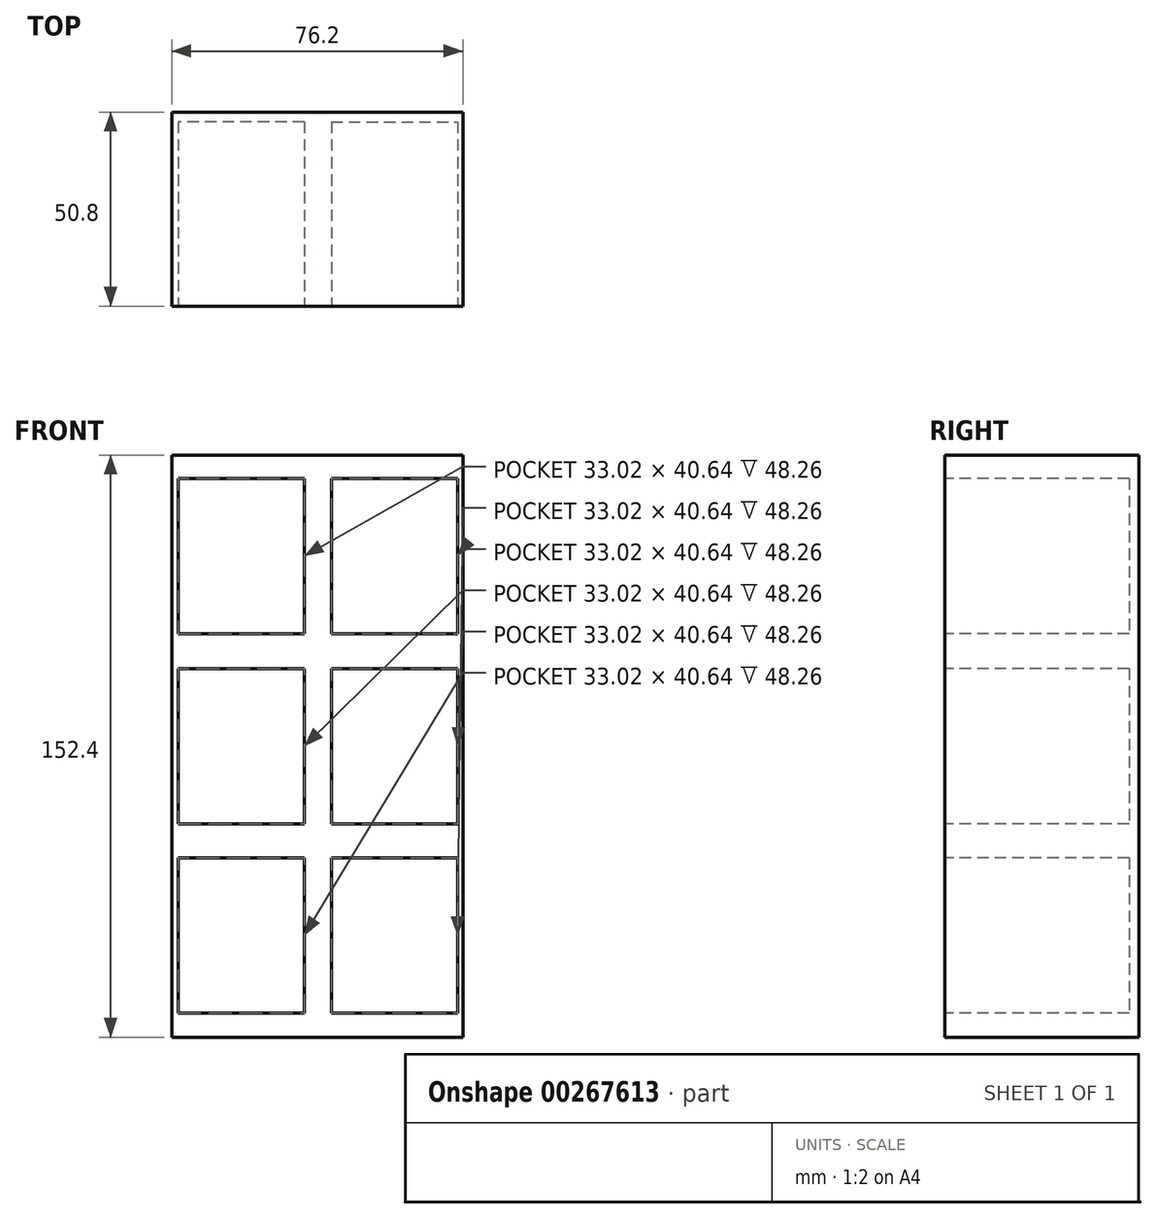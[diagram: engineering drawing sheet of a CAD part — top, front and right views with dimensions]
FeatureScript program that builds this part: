
annotation { "Feature Type Name" : "Feature", "Feature Type Description" : "" }
export const myFeature = defineFeature(function(context is Context, id is Id, definition is map)
    precondition{}
    {
        {
            var Q0;
            Q0=qCreatedBy(makeId("Front.planeOp"),FACE);
            var sketch = newSketch(context, id + "F0", { "sketchPlane" : qUnion([Q0])});
            skLineSegment(sketch, "E0.bottom", {"start": v(38.1, 76.2) * mm, "end": v(-38.1, 76.2) * mm});
            skLineSegment(sketch, "E0.top", {"start": v(38.1, -76.2) * mm, "end": v(-38.1, -76.2) * mm});
            skLineSegment(sketch, "E0.left", {"start": v(38.1, 76.2) * mm, "end": v(38.1, -76.2) * mm});
            skLineSegment(sketch, "E0.right", {"start": v(-38.1, 76.2) * mm, "end": v(-38.1, -76.2) * mm});
            skPoint(sketch, "E0.middle", {"position": v(0, 0) * mm});
            skSolve(sketch);
        }
        {
            var Q0;
            Q0 = qSketchRegion(id + "F0", true);
            extrude(context, id + "F1", {"entities" : qUnion([Q0]), "depth" : 50.8 * mm});
        }
        {
            var Q0;
            Q0=makeQuery(id+"F1.opExtrude","CAP_FACE",FACE,{"disambiguationData":[OSD([sQuery(id+"F0.wireOp",EDGE,"E0.bottom"),sQuery(id+"F0.wireOp",EDGE,"E0.top"),sQuery(id+"F0.wireOp",EDGE,"E0.left"),sQuery(id+"F0.wireOp",EDGE,"E0.right")])],"isStart":false});
            var sketch = newSketch(context, id + "F2", { "sketchPlane" : qUnion([Q0])});
            skLineSegment(sketch, "E1.bottom", {"start": v(-3.37, 70.1) * mm, "end": v(-36.4, 70.1) * mm});
            skLineSegment(sketch, "E1.top", {"start": v(-3.37, 29.47) * mm, "end": v(-36.4, 29.47) * mm});
            skLineSegment(sketch, "E1.left", {"start": v(-3.37, 70.1) * mm, "end": v(-3.37, 29.47) * mm});
            skLineSegment(sketch, "E1.right", {"start": v(-36.4, 70.1) * mm, "end": v(-36.4, 29.47) * mm});
            skPoint(sketch, "E1.middle", {"position": v(-19.88, 49.79) * mm});
            skLineSegment(sketch, "E2.bottom", {"start": v(3.7, 70.1) * mm, "end": v(36.72, 70.1) * mm});
            skLineSegment(sketch, "E2.top", {"start": v(3.7, 29.47) * mm, "end": v(36.72, 29.47) * mm});
            skLineSegment(sketch, "E2.left", {"start": v(3.7, 70.1) * mm, "end": v(3.7, 29.47) * mm});
            skLineSegment(sketch, "E2.right", {"start": v(36.72, 70.1) * mm, "end": v(36.72, 29.47) * mm});
            skPoint(sketch, "E2.middle", {"position": v(20.21, 49.79) * mm});
            skLineSegment(sketch, "E3.bottom", {"start": v(-3.37, 20.32) * mm, "end": v(-36.4, 20.32) * mm});
            skLineSegment(sketch, "E3.top", {"start": v(-3.37, -20.32) * mm, "end": v(-36.4, -20.32) * mm});
            skLineSegment(sketch, "E3.left", {"start": v(-3.37, 20.32) * mm, "end": v(-3.37, -20.32) * mm});
            skLineSegment(sketch, "E3.right", {"start": v(-36.4, 20.32) * mm, "end": v(-36.4, -20.32) * mm});
            skPoint(sketch, "E3.middle", {"position": v(-19.88, 0) * mm});
            skLineSegment(sketch, "E4.bottom", {"start": v(3.7, 20.32) * mm, "end": v(36.72, 20.32) * mm});
            skLineSegment(sketch, "E4.top", {"start": v(3.7, -20.32) * mm, "end": v(36.72, -20.32) * mm});
            skLineSegment(sketch, "E4.left", {"start": v(3.7, 20.32) * mm, "end": v(3.7, -20.32) * mm});
            skLineSegment(sketch, "E4.right", {"start": v(36.72, 20.32) * mm, "end": v(36.72, -20.32) * mm});
            skPoint(sketch, "E4.middle", {"position": v(20.21, 0) * mm});
            skPoint(sketch, "E4.middle.positionSnap0", {"position": v(20.21, 29.47) * mm});
            skPoint(sketch, "E4.centerSnap0", {"position": v(20.21, 29.47) * mm});
            skLineSegment(sketch, "E5.bottom", {"start": v(-3.37, -29.28) * mm, "end": v(-36.4, -29.28) * mm});
            skLineSegment(sketch, "E5.top", {"start": v(-3.37, -69.92) * mm, "end": v(-36.4, -69.92) * mm});
            skLineSegment(sketch, "E5.left", {"start": v(-3.37, -29.28) * mm, "end": v(-3.37, -69.92) * mm});
            skLineSegment(sketch, "E5.right", {"start": v(-36.4, -29.28) * mm, "end": v(-36.4, -69.92) * mm});
            skPoint(sketch, "E5.middle", {"position": v(-19.88, -49.6) * mm});
            skLineSegment(sketch, "E6.bottom", {"start": v(3.7, -29.28) * mm, "end": v(36.72, -29.28) * mm});
            skLineSegment(sketch, "E6.top", {"start": v(3.7, -69.92) * mm, "end": v(36.72, -69.92) * mm});
            skLineSegment(sketch, "E6.left", {"start": v(3.7, -29.28) * mm, "end": v(3.7, -69.92) * mm});
            skLineSegment(sketch, "E6.right", {"start": v(36.72, -29.28) * mm, "end": v(36.72, -69.92) * mm});
            skPoint(sketch, "E6.middle", {"position": v(20.21, -49.6) * mm});
            skPoint(sketch, "E6.middle.positionSnap0", {"position": v(20.21, -20.32) * mm});
            skPoint(sketch, "E6.centerSnap0", {"position": v(20.21, -20.32) * mm});
            skSolve(sketch);
        }
        {
            var Q0;
            Q0 = qSketchRegion(id + "F2", true);
            extrude(context, id + "F3", {"entities" : qUnion([Q0]), "operationType" : NewBodyOperationType.REMOVE, "oppositeDirection" : true, "depth" : 48.26 * mm});
        }
    });
